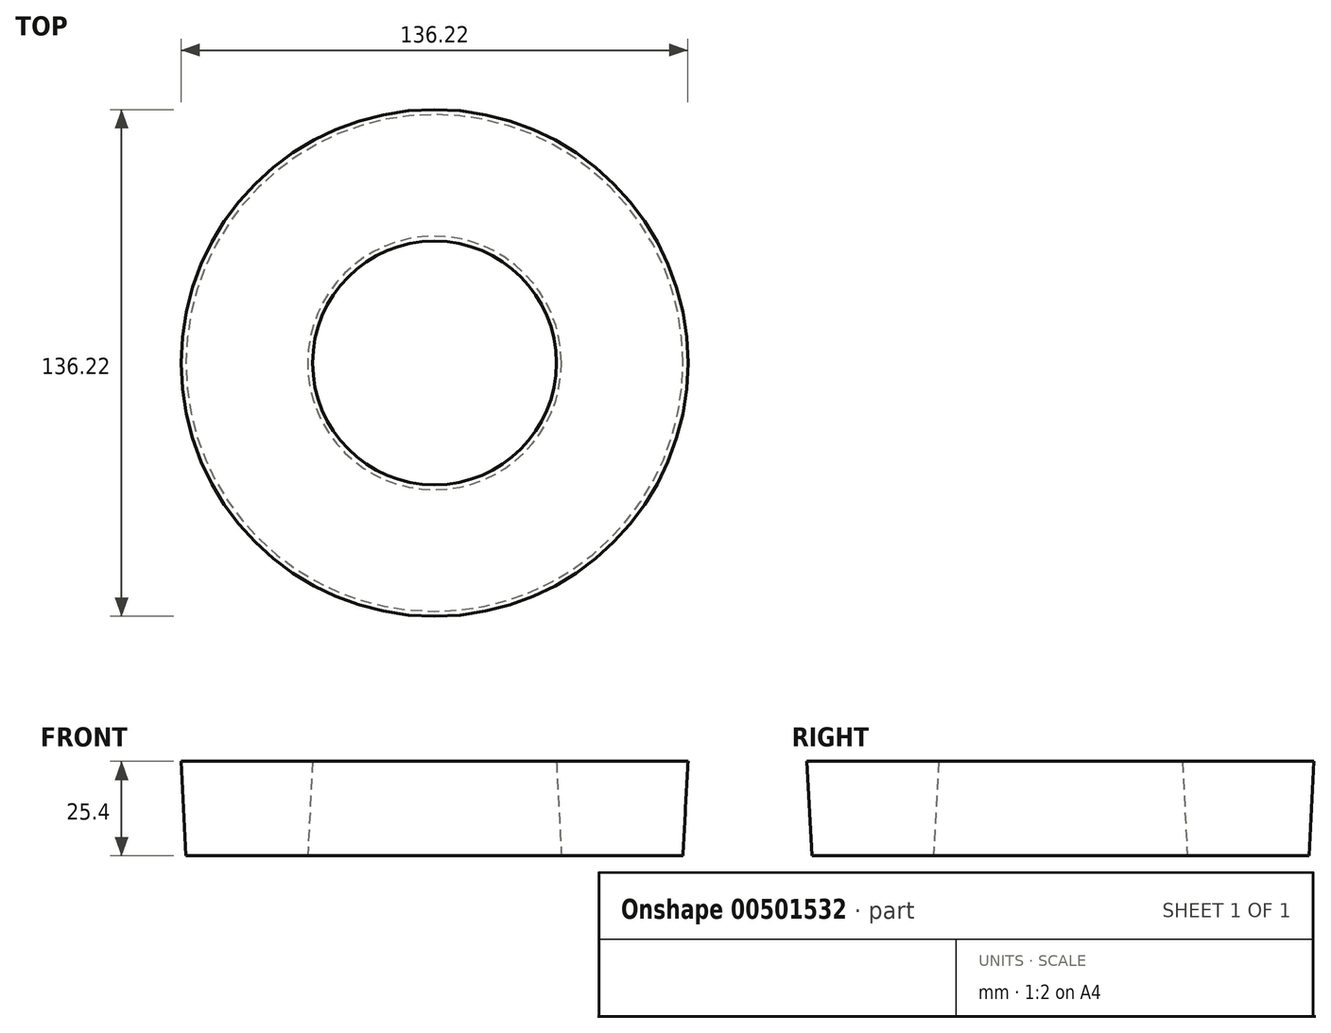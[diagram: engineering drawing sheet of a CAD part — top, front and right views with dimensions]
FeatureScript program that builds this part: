
annotation { "Feature Type Name" : "Feature", "Feature Type Description" : "" }
export const myFeature = defineFeature(function(context is Context, id is Id, definition is map)
    precondition{}
    {
        {
            var Q0;
            Q0=qCreatedBy(makeId("Top.planeOp"),FACE);
            var sketch = newSketch(context, id + "F0", { "sketchPlane" : qUnion([Q0])});
            skCircle(sketch, "E0", {"center": v(0, 0) * mm, "radius": 66.78 * mm});
            skCircle(sketch, "E1", {"center": v(0, 0) * mm, "radius": 34.1 * mm});
            skSolve(sketch);
        }
        {
            var Q0;
            Q0 = qSketchRegion(id + "F0", true);
            extrude(context, id + "F1", {"entities" : qUnion([Q0]), "depth" : 25.4 * mm, "hasDraft" : true, "draftAngle" : 3 * degree});
        }
    });
